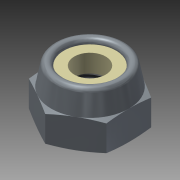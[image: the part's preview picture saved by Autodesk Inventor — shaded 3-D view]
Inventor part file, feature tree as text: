
AUTODESK INVENTOR PART (.ipt)
format: ipt  version: 2013 (Build 170138000, 138)  size: 200,704 bytes
history: native  units: mm (DEFAULTED — no unit token found)
features: sketch x5, extrude x2, revolve x2, other x1, plane x1, thread x1
ambient origin geometry x8: Origin, YZ Plane, XZ Plane, XY Plane, X Axis, Y Axis, Z Axis, Center Point
bodies: Solid1 (feature_tree)
feature tree (12):
  other  "Hexagon_flats_join1"
  extrude  "Extrusion1"  Depth=25.4mm TaperAngle=0.0deg
  revolve  "Revolution1"  Angle=90.0deg
  plane  "Work Plane1"
  extrude  "Extrusion2"  Depth=1.566333mm
  revolve  "Revolution2"  Angle=15.0deg
  thread  "Thread1"  [1 undecoded]
  sketch  "Sketch1"  dims[d0=9.525mm d3=25.4mm d4=0.0mm]
  sketch  "Sketch2"  dims[d5=13.788101mm d7=90.0deg]
  sketch  "Sketch3"  dims[d9=25.4mm d10=0.0mm d11=1.566333mm]
  sketch  "Sketch4"  dims[d12=15.0deg d13=15.0deg d14=9.525mm]
  sketch  "Sketch5"  dims[d15=90.0deg d16=25.4mm d17=0.0mm]
note: 1 required parameter value undecoded (feature->parameter linkage not recoverable at this tier; creation-order binding heuristic only, values carry confidence <= 0.55)
